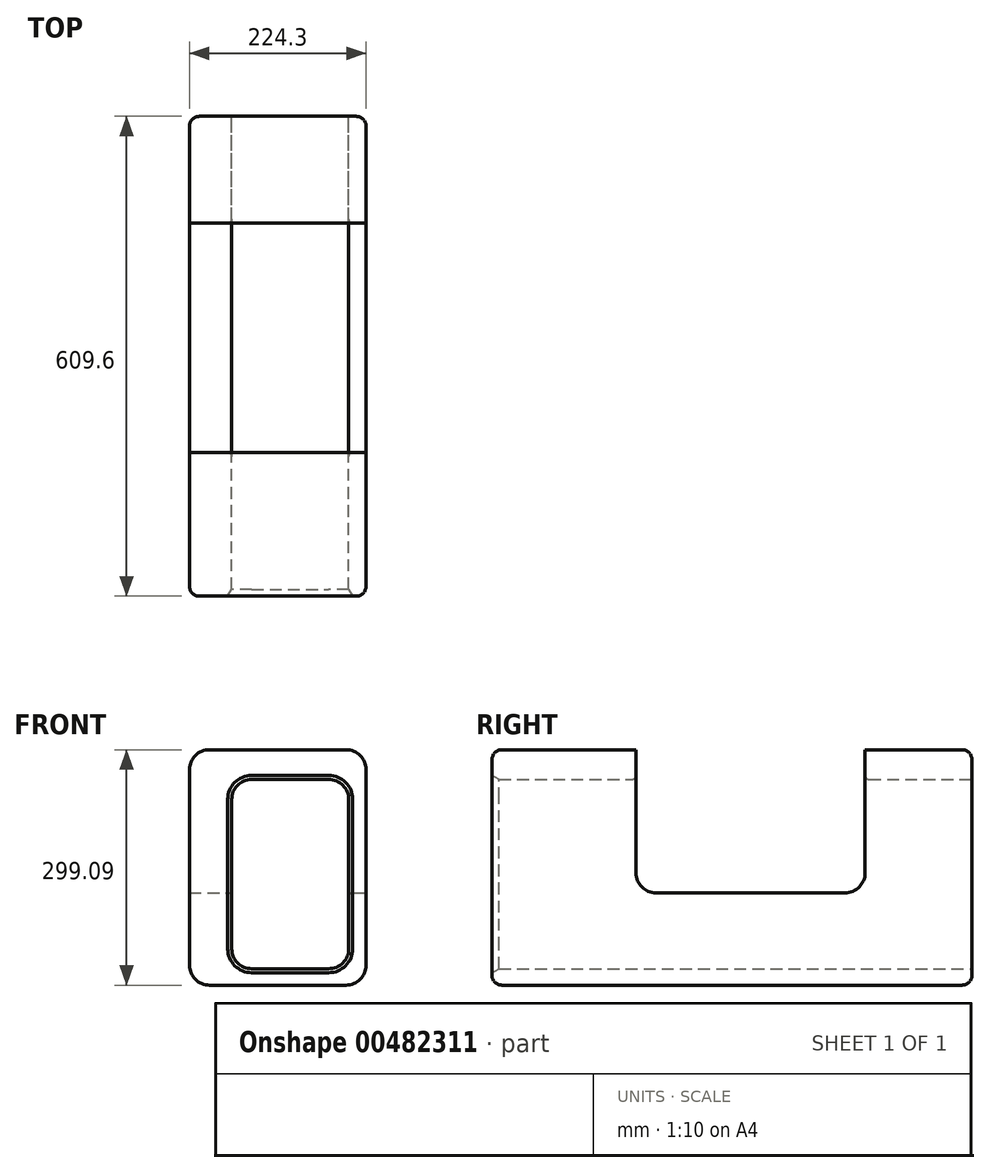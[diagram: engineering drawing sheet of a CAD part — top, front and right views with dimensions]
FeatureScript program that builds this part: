
annotation { "Feature Type Name" : "Feature", "Feature Type Description" : "" }
export const myFeature = defineFeature(function(context is Context, id is Id, definition is map)
    precondition{}
    {
        {
            var Q0;
            Q0=qCreatedBy(makeId("Front.planeOp"),FACE);
            var sketch = newSketch(context, id + "F0", { "sketchPlane" : qUnion([Q0])});
            skLineSegment(sketch, "E0.bottom", {"start": v(39, -117.23) * mm, "end": v(263.29, -117.23) * mm});
            skLineSegment(sketch, "E0.top", {"start": v(39, 181.86) * mm, "end": v(263.29, 181.86) * mm});
            skLineSegment(sketch, "E0.left", {"start": v(39, -117.23) * mm, "end": v(39, 181.86) * mm});
            skLineSegment(sketch, "E0.right", {"start": v(263.29, -117.23) * mm, "end": v(263.29, 181.86) * mm});
            skLineSegment(sketch, "E1.bottom", {"start": v(241.26, -96.33) * mm, "end": v(92.65, -96.33) * mm});
            skLineSegment(sketch, "E1.top", {"start": v(241.26, 144.1) * mm, "end": v(92.65, 144.1) * mm});
            skLineSegment(sketch, "E1.left", {"start": v(241.26, -96.33) * mm, "end": v(241.26, 144.1) * mm});
            skLineSegment(sketch, "E1.right", {"start": v(92.65, -96.33) * mm, "end": v(92.65, 144.1) * mm});
            skSolve(sketch);
        }
        {
            var Q0;
            Q0=makeQuery(id+"F0.imprint","IMPRINT",FACE,{"disambiguationData":[TD([[makeQuery(id+"F0.imprint","IMPRINT",EDGE,{"derivedFrom":sQuery(id+"F0.wireOp",EDGE,"E0.bottom")}),1.0]])]});
            extrude(context, id + "F1", {"entities" : qUnion([Q0]), "depth" : 609.6 * mm});
        }
        {
            var Q0;
            Q0=makeQuery(id+"F1.opExtrude","SWEPT_EDGE",EDGE,{"disambiguationData":[OSD([sQuery(id+"F0.wireOp",EDGE,"E1.bottom"),sQuery(id+"F0.wireOp",EDGE,"E1.right")])]});
            var Q1;
            Q1=makeQuery(id+"F1.opExtrude","SWEPT_EDGE",EDGE,{"disambiguationData":[OSD([sQuery(id+"F0.wireOp",EDGE,"E1.bottom"),sQuery(id+"F0.wireOp",EDGE,"E1.left")])]});
            var Q2;
            Q2=makeQuery(id+"F1.opExtrude","SWEPT_EDGE",EDGE,{"disambiguationData":[OSD([sQuery(id+"F0.wireOp",EDGE,"E1.top"),sQuery(id+"F0.wireOp",EDGE,"E1.right")])]});
            var Q3;
            Q3=makeQuery(id+"F1.opExtrude","SWEPT_EDGE",EDGE,{"disambiguationData":[OSD([sQuery(id+"F0.wireOp",EDGE,"E1.top"),sQuery(id+"F0.wireOp",EDGE,"E1.left")])]});
            fillet(context, id + "F2", {"entities" : qUnion([Q0, Q1, Q2, Q3]), "radius" : 25.4 * mm, "tangentPropagation" : true, "allowEdgeOverflow" : false});
        }
        {
            var Q0;
            Q0=makeQuery(id+"F1.opExtrude","SWEPT_EDGE",EDGE,{"disambiguationData":[OSD([sQuery(id+"F0.wireOp",EDGE,"E0.top"),sQuery(id+"F0.wireOp",EDGE,"E0.right")])]});
            var Q1;
            Q1=makeQuery(id+"F1.opExtrude","SWEPT_EDGE",EDGE,{"disambiguationData":[OSD([sQuery(id+"F0.wireOp",EDGE,"E0.top"),sQuery(id+"F0.wireOp",EDGE,"E0.left")])]});
            var Q2;
            Q2=makeQuery(id+"F1.opExtrude","SWEPT_EDGE",EDGE,{"disambiguationData":[OSD([sQuery(id+"F0.wireOp",EDGE,"E0.bottom"),sQuery(id+"F0.wireOp",EDGE,"E0.right")])]});
            var Q3;
            Q3=makeQuery(id+"F1.opExtrude","SWEPT_EDGE",EDGE,{"disambiguationData":[OSD([sQuery(id+"F0.wireOp",EDGE,"E0.bottom"),sQuery(id+"F0.wireOp",EDGE,"E0.left")])]});
            fillet(context, id + "F3", {"entities" : qUnion([Q0, Q1, Q2, Q3]), "radius" : 25.4 * mm, "tangentPropagation" : true, "allowEdgeOverflow" : false});
        }
        {
            var Q0;
            Q0=makeQuery(id+"F1.opExtrude","CAP_EDGE",EDGE,{"disambiguationData":[OSD([sQuery(id+"F0.wireOp",EDGE,"E0.top")])],"isStart":false});
            fillet(context, id + "F4", {"entities" : qUnion([Q0]), "radius" : 12.7 * mm, "tangentPropagation" : true, "allowEdgeOverflow" : false});
        }
        {
            var Q0;
            Q0=makeQuery(id+"F1.opExtrude","CAP_EDGE",EDGE,{"disambiguationData":[OSD([sQuery(id+"F0.wireOp",EDGE,"E0.top")])],"isStart":true});
            fillet(context, id + "F5", {"entities" : qUnion([Q0]), "radius" : 12.7 * mm, "tangentPropagation" : true, "allowEdgeOverflow" : false});
        }
        {
            var Q0;
            Q0=makeQuery(id+"F1.opExtrude","SWEPT_FACE",FACE,{"disambiguationData":[OSD([sQuery(id+"F0.wireOp",EDGE,"E0.right")])]});
            var sketch = newSketch(context, id + "F6", { "sketchPlane" : qUnion([Q0])});
            skLineSegment(sketch, "E2.bottom", {"start": v(-135.72, 387.56) * mm, "end": v(-426.74, 387.56) * mm});
            skLineSegment(sketch, "E2.top", {"start": v(-135.72, 0) * mm, "end": v(-426.74, 0) * mm});
            skLineSegment(sketch, "E2.left", {"start": v(-135.72, 387.56) * mm, "end": v(-135.72, 0) * mm});
            skLineSegment(sketch, "E2.right", {"start": v(-426.74, 387.56) * mm, "end": v(-426.74, 0) * mm});
            skSolve(sketch);
        }
        {
            var Q0;
            Q0 = qSketchRegion(id + "F6", true);
            var Q1;
            Q1=makeQuery(id+"F1.opExtrude","SWEPT_FACE",FACE,{"disambiguationData":[OSD([sQuery(id+"F0.wireOp",EDGE,"E0.right")])]});
            var Q2;
            Q2=makeQuery(id+"F1.opExtrude","SWEPT_BODY",BODY,{"disambiguationData":[OSD([sQuery(id+"F0.wireOp",EDGE,"E0.bottom"),sQuery(id+"F0.wireOp",EDGE,"E0.top"),sQuery(id+"F0.wireOp",EDGE,"E0.left"),sQuery(id+"F0.wireOp",EDGE,"E0.right"),sQuery(id+"F0.wireOp",EDGE,"E1.bottom"),sQuery(id+"F0.wireOp",EDGE,"E1.top"),sQuery(id+"F0.wireOp",EDGE,"E1.left"),sQuery(id+"F0.wireOp",EDGE,"E1.right")])]});
            extrude(context, id + "F7", {"entities" : qUnion([Q0]), "operationType" : NewBodyOperationType.REMOVE, "endBound" : BoundingType.UP_TO_BODY, "oppositeDirection" : true, "endBoundEntityFace" : qUnion([Q1]), "endBoundEntityBody" : qUnion([Q2]), "depth" : 25.4 * mm});
        }
        {
            var Q0;
            {var subQ0=sQuery(id+"F6.wireOp",EDGE,"E2.left");var subQ1=sQuery(id+"F6.wireOp",EDGE,"E2.top");Q0=makeQuery(id+"F7.boolean.opBoolean","COPY",EDGE,{"disambiguationData":[TD([makeQuery(id+"F1.opExtrude","SWEPT_FACE",FACE,{"disambiguationData":[OSD([sQuery(id+"F0.wireOp",EDGE,"E0.left")])]})])],"derivedFrom":makeQuery(id+"F7.opExtrude","SWEPT_EDGE",EDGE,{"disambiguationData":[OSD([subQ1,subQ0])]})});}
            var Q1;
            {var subQ0=sQuery(id+"F6.wireOp",EDGE,"E2.top");var subQ1=sQuery(id+"F6.wireOp",EDGE,"E2.left");Q1=makeQuery(id+"F7.boolean.opBoolean","COPY",EDGE,{"disambiguationData":[TD([makeQuery(id+"F1.opExtrude","SWEPT_FACE",FACE,{"disambiguationData":[OSD([sQuery(id+"F0.wireOp",EDGE,"E0.right")])]})])],"derivedFrom":makeQuery(id+"F7.opExtrude","SWEPT_EDGE",EDGE,{"disambiguationData":[OSD([subQ0,subQ1])]})});}
            var Q2;
            {var subQ0=sQuery(id+"F6.wireOp",EDGE,"E2.top");var subQ1=sQuery(id+"F6.wireOp",EDGE,"E2.right");Q2=makeQuery(id+"F7.boolean.opBoolean","COPY",EDGE,{"disambiguationData":[TD([makeQuery(id+"F1.opExtrude","SWEPT_FACE",FACE,{"disambiguationData":[OSD([sQuery(id+"F0.wireOp",EDGE,"E0.left")])]})])],"derivedFrom":makeQuery(id+"F7.opExtrude","SWEPT_EDGE",EDGE,{"disambiguationData":[OSD([subQ0,subQ1])]})});}
            var Q3;
            {var subQ0=sQuery(id+"F6.wireOp",EDGE,"E2.right");var subQ1=sQuery(id+"F6.wireOp",EDGE,"E2.top");Q3=makeQuery(id+"F7.boolean.opBoolean","COPY",EDGE,{"disambiguationData":[TD([makeQuery(id+"F1.opExtrude","SWEPT_FACE",FACE,{"disambiguationData":[OSD([sQuery(id+"F0.wireOp",EDGE,"E0.right")])]})])],"derivedFrom":makeQuery(id+"F7.opExtrude","SWEPT_EDGE",EDGE,{"disambiguationData":[OSD([subQ1,subQ0])]})});}
            fillet(context, id + "F8", {"entities" : qUnion([Q0, Q1, Q2, Q3]), "radius" : 25.4 * mm, "tangentPropagation" : true, "allowEdgeOverflow" : false});
        }
        {
            var Q0;
            Q0=makeQuery(id+"F7.boolean.opBoolean","COPY",EDGE,{"derivedFrom":makeQuery(id+"F7.opExtrude","CAP_EDGE",EDGE,{"disambiguationData":[OSD([sQuery(id+"F6.wireOp",EDGE,"E2.top")])],"isStart":false})});
            var Q1;
            Q1=makeQuery(id+"F7.boolean.opBoolean","INTERSECT",EDGE,{"derivedFrom":[makeQuery(id+"F1.opExtrude","SWEPT_FACE",FACE,{"disambiguationData":[OSD([sQuery(id+"F0.wireOp",EDGE,"E1.right")])]}),makeQuery(id+"F7.opExtrude","SWEPT_FACE",FACE,{"disambiguationData":[OSD([sQuery(id+"F6.wireOp",EDGE,"E2.top")])]})]});
            fillet(context, id + "F9", {"entities" : qUnion([Q0, Q1]), "radius" : 5.08 * mm, "tangentPropagation" : true, "allowEdgeOverflow" : false});
        }
        {
            var Q0;
            Q0=makeQuery(id+"F1.opExtrude","CAP_EDGE",EDGE,{"disambiguationData":[OSD([sQuery(id+"F0.wireOp",EDGE,"E1.bottom")])],"isStart":false});
            chamfer(context, id + "F10", {"entities" : qUnion([Q0]), "chamferType" : ChamferType.OFFSET_ANGLE, "width" : 5.08 * mm, "oppositeDirection" : false, "angle" : 60 * degree, "tangentPropagation" : true});
        }
    });
